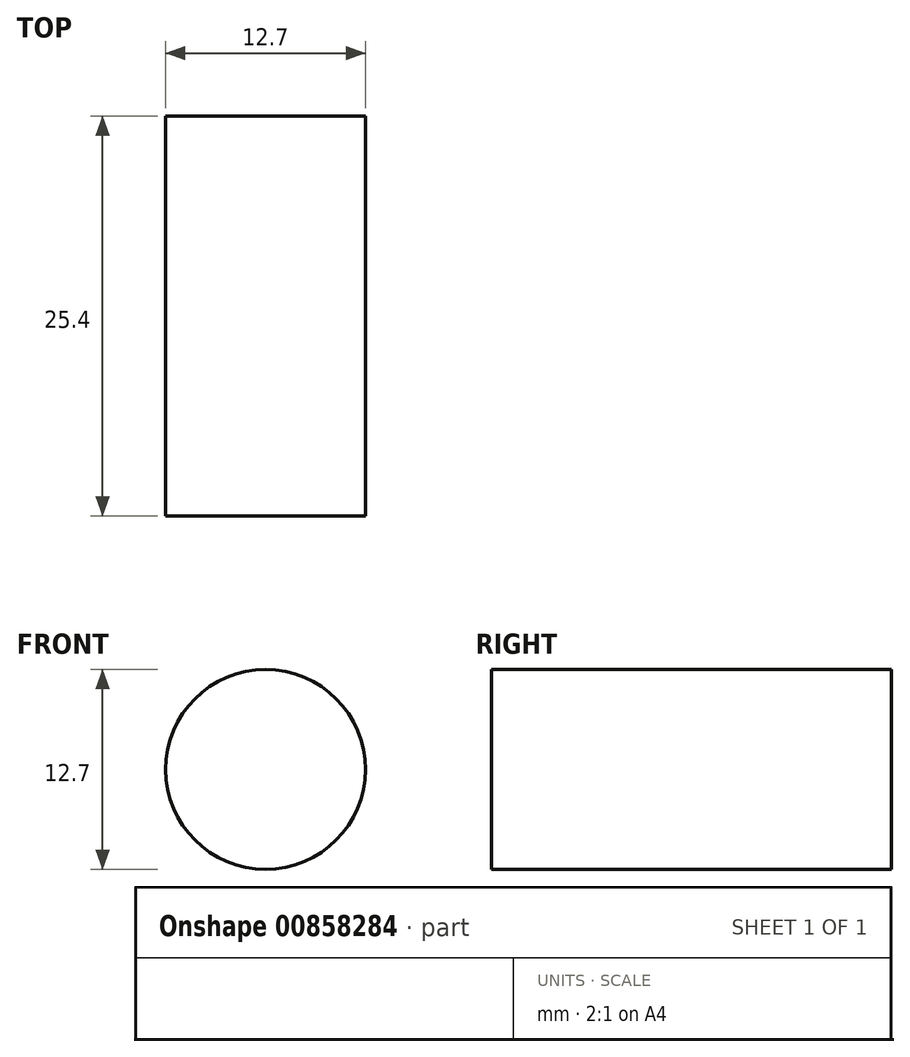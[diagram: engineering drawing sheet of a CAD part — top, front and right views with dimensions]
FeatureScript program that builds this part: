
annotation { "Feature Type Name" : "Feature", "Feature Type Description" : "" }
export const myFeature = defineFeature(function(context is Context, id is Id, definition is map)
    precondition{}
    {
        {
            var Q0;
            Q0=qCreatedBy(makeId("Front.planeOp"),FACE);
            var sketch = newSketch(context, id + "F0", { "sketchPlane" : qUnion([Q0])});
            skCircle(sketch, "E0", {"center": v(0, 0) * mm, "radius": 6.35 * mm});
            skSolve(sketch);
        }
        {
            var Q0;
            Q0=makeQuery(id+"F0.imprint","IMPRINT",FACE,{"disambiguationData":[TD([[makeQuery(id+"F0.imprint","IMPRINT",EDGE,{"derivedFrom":sQuery(id+"F0.wireOp",EDGE,"E0")}),1.0]])]});
            extrude(context, id + "F1", {"entities" : qUnion([Q0]), "depth" : 25.4 * mm, "offsetDistance" : 25.4 * mm, "symmetric" : true});
        }
    });
